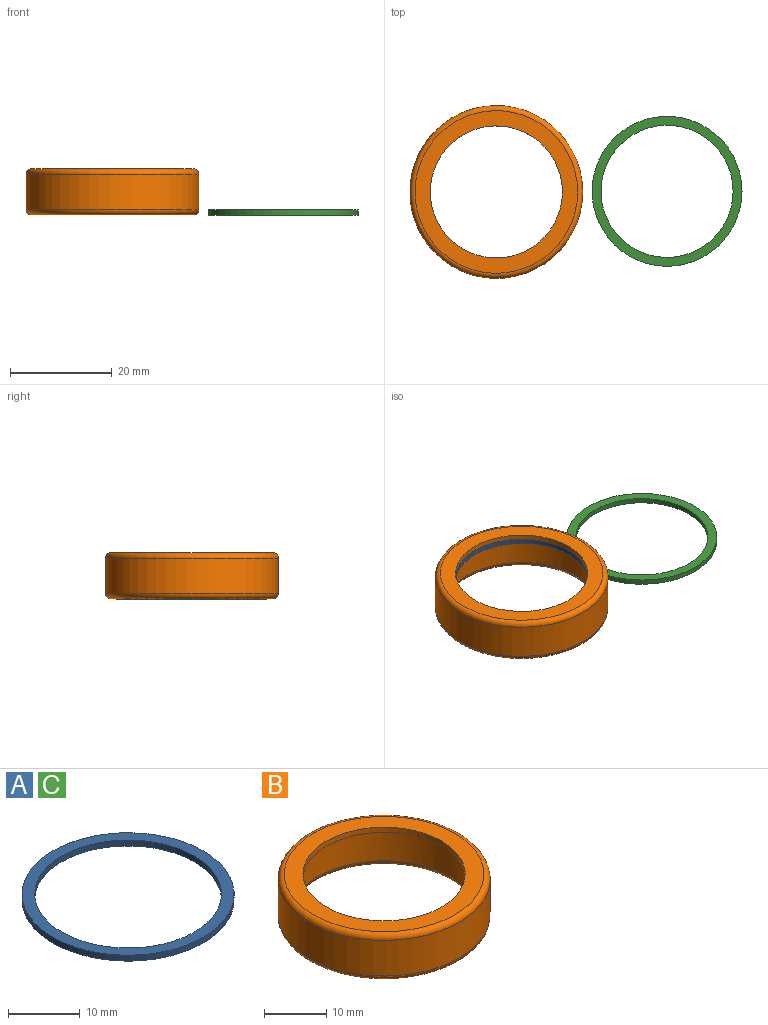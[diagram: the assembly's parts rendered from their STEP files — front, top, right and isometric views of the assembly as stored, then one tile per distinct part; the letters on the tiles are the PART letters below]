
ASSEMBLY  parts=3 mates=1
PART A: 4 faces, bbox 29.5x29.5x1 mm
  f0: cylinder r=14.75mm len=29.5mm, axis (0,0,-1), area 92.7mm2, adj f1,f2
  f1: plane 29.5x29.5mm, normal (0,0,1), area 152.6mm2, adj f0,f3
  f2: plane 29.5x29.5mm, normal (0,0,-1), area 152.6mm2, adj f0,f3
  f3: cylinder r=13mm len=26mm, axis (0,0,-1), area 81.7mm2, adj f1,f2
PART B: 7 faces, bbox 36.8x36.8x9 mm
  f0: cylinder r=17mm len=34mm, axis (0,0,-1), area 747.7mm2, adj f5,f6
  f1: cylinder r=15mm len=30mm, axis (0,0,-1), area 659.7mm2, adj f2,f5
  f2: plane 30x30mm, normal (0,0,-1), area 175.9mm2, adj f1,f4
  f3: plane 32x32mm, normal (0,0,1), area 273.3mm2, adj f4,f6
  f4: cylinder r=13mm len=26mm, axis (0,0,1), area 81.7mm2, adj f2,f3
  f5: torus R=16mm, axis (0,0,1), area 315.8mm2, adj f0,f1
  f6: torus R=16mm, axis (0,0,1), area 164.2mm2, adj f0,f3
PART C: same geometry as A
PLACE A t=(-19.57,-12.72,6.59)mm
PLACE B t=(-19.57,-12.72,-0.41)mm
PLACE C t=(14.03,-12.57,-0.49)mm
MATE fastened A.f0 <-> B.f1  axis (0,0,1) through (-19.57,-12.72,7.59)mm
